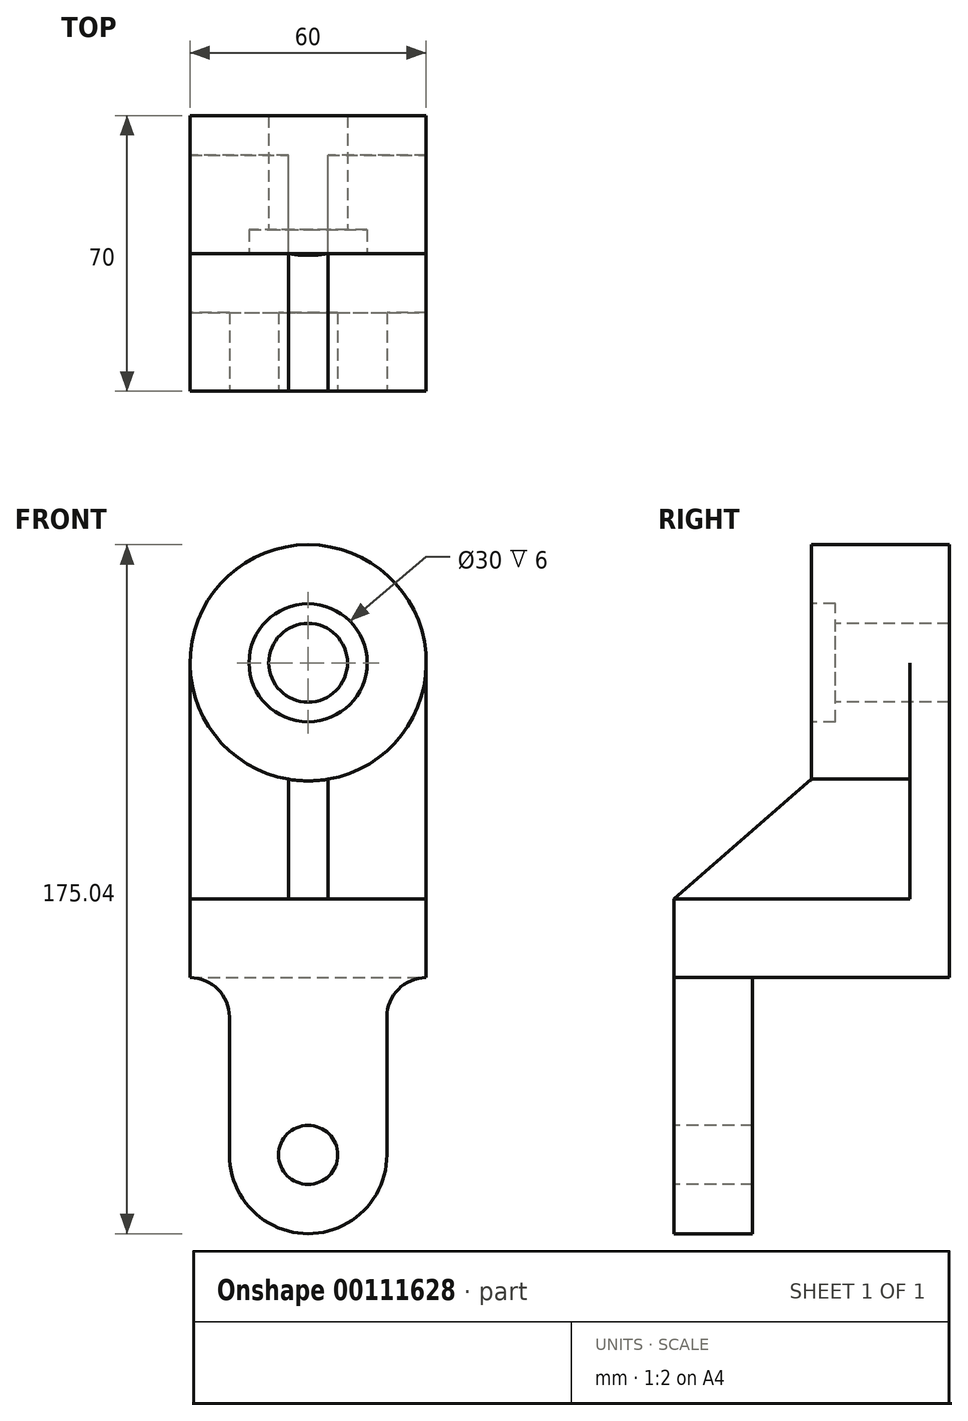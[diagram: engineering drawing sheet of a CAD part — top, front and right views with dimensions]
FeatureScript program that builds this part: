
annotation { "Feature Type Name" : "Feature", "Feature Type Description" : "" }
export const myFeature = defineFeature(function(context is Context, id is Id, definition is map)
    precondition{}
    {
        {
            var Q0;
            Q0=qCreatedBy(makeId("Top.planeOp"),FACE);
            var sketch = newSketch(context, id + "F0", { "sketchPlane" : qUnion([Q0])});
            skLineSegment(sketch, "E0.bottom", {"start": v(-34.23, 8.14) * mm, "end": v(25.77, 8.14) * mm});
            skLineSegment(sketch, "E0.top", {"start": v(-34.23, -61.86) * mm, "end": v(25.77, -61.86) * mm});
            skLineSegment(sketch, "E0.left", {"start": v(-34.23, 8.14) * mm, "end": v(-34.23, -61.86) * mm});
            skLineSegment(sketch, "E0.right", {"start": v(25.77, 8.14) * mm, "end": v(25.77, -61.86) * mm});
            skPoint(sketch, "E1", {"position": v(-4.23, 8.14) * mm});
            skSolve(sketch);
        }
        {
            var Q0;
            Q0 = qSketchRegion(id + "F0", true);
            extrude(context, id + "F1", {"entities" : qUnion([Q0]), "depth" : 20 * mm});
        }
        {
            var Q0;
            Q0=makeQuery(id+"F1.opExtrude","SWEPT_FACE",FACE,{"disambiguationData":[OSD([sQuery(id+"F0.wireOp",EDGE,"E0.bottom")])]});
            var sketch = newSketch(context, id + "F2", { "sketchPlane" : qUnion([Q0])});
            skPoint(sketch, "E2", {"position": v(4.23, 0) * mm});
            skLineSegment(sketch, "E3", {"start": v(-25.77, 20) * mm, "end": v(-25.77, 80) * mm});
            skLineSegment(sketch, "E4", {"start": v(34.23, 20) * mm, "end": v(34.23, 80) * mm});
            skLineSegment(sketch, "E5", {"start": v(-25.77, 20) * mm, "end": v(34.23, 20) * mm});
            skArc(sketch, "E6", {"start": v(34.23, 80) * mm, "mid": v(4.23, 110) * mm, "end": v(-25.77, 80) * mm});
            skSolve(sketch);
        }
        {
            var Q0;
            Q0 = qSketchRegion(id + "F2", true);
            extrude(context, id + "F3", {"entities" : qUnion([Q0]), "operationType" : NewBodyOperationType.ADD, "oppositeDirection" : true, "depth" : 10 * mm});
        }
        {
            var Q0;
            Q0=makeQuery(id+"F3.opExtrude","CAP_FACE",FACE,{"disambiguationData":[OSD([sQuery(id+"F2.wireOp",EDGE,"E3"),sQuery(id+"F2.wireOp",EDGE,"E4"),sQuery(id+"F2.wireOp",EDGE,"E5"),sQuery(id+"F2.wireOp",EDGE,"E6")])],"isStart":false});
            var sketch = newSketch(context, id + "F4", { "sketchPlane" : qUnion([Q0])});
            skPoint(sketch, "E7", {"position": v(-4.23, 80) * mm});
            skCircle(sketch, "E8", {"center": v(-4.23, 80) * mm, "radius": 30 * mm});
            skSolve(sketch);
        }
        {
            var Q0;
            Q0 = qSketchRegion(id + "F4", true);
            extrude(context, id + "F5", {"entities" : qUnion([Q0]), "operationType" : NewBodyOperationType.ADD, "depth" : 25 * mm});
        }
        {
            var Q0;
            Q0=makeQuery(id+"F5.opExtrude","CAP_FACE",FACE,{"disambiguationData":[OSD([sQuery(id+"F4.wireOp",EDGE,"E8")])],"isStart":false});
            var sketch = newSketch(context, id + "F6", { "sketchPlane" : qUnion([Q0])});
            skPoint(sketch, "E9", {"position": v(-4.23, 80) * mm});
            skSolve(sketch);
        }
        {
            var Q0;
            Q0=sQuery(id+"F6.wireOp",VERTEX,"E9");
            var Q1;
            Q1=makeQuery(id+"F1.opExtrude","SWEPT_BODY",BODY,{"disambiguationData":[OSD([sQuery(id+"F0.wireOp",EDGE,"E0.bottom"),sQuery(id+"F0.wireOp",EDGE,"E0.top"),sQuery(id+"F0.wireOp",EDGE,"E0.left"),sQuery(id+"F0.wireOp",EDGE,"E0.right")])]});
            hole(context, id + "F7", {"style" : HoleStyle.C_BORE, "endStyle" : HoleEndStyle.BLIND, "holeDiameter" : 20 * mm, "cBoreDiameter" : 30 * mm, "cBoreDepth" : 6 * mm, "holeDepth" : 50 * mm, "startFromSketch" : true, "locations" : qUnion([Q0]), "scope" : qUnion([Q1])});
        }
        {
            var Q0;
            Q0=makeQuery(id+"F1.opExtrude","CAP_FACE",FACE,{"disambiguationData":[OSD([sQuery(id+"F0.wireOp",EDGE,"E0.bottom"),sQuery(id+"F0.wireOp",EDGE,"E0.top"),sQuery(id+"F0.wireOp",EDGE,"E0.left"),sQuery(id+"F0.wireOp",EDGE,"E0.right")])],"isStart":false});
            var sketch = newSketch(context, id + "F8", { "sketchPlane" : qUnion([Q0])});
            skPoint(sketch, "E10.endSnap0", {"position": v(-4.23, -61.86) * mm});
            skLineSegment(sketch, "E11.bottom", {"start": v(0.77, -61.86) * mm, "end": v(-9.23, -61.86) * mm});
            skLineSegment(sketch, "E11.top", {"start": v(0.77, -1.86) * mm, "end": v(-9.23, -1.86) * mm});
            skLineSegment(sketch, "E11.left", {"start": v(0.77, -61.86) * mm, "end": v(0.77, -1.86) * mm});
            skLineSegment(sketch, "E11.right", {"start": v(-9.23, -61.86) * mm, "end": v(-9.23, -1.86) * mm});
            skSolve(sketch);
        }
        {
            var Q0;
            Q0 = qSketchRegion(id + "F8", true);
            var Q1;
            Q1=makeQuery(id+"F5.boolean.opBoolean","MERGE",FACE,{"derivedFrom":[makeQuery(id+"F3.opExtrude","SWEPT_FACE",FACE,{"disambiguationData":[OSD([sQuery(id+"F2.wireOp",EDGE,"E6")])]}),makeQuery(id+"F5.opExtrude","SWEPT_FACE",FACE,{"disambiguationData":[OSD([sQuery(id+"F4.wireOp",EDGE,"E8")])]})]});
            extrude(context, id + "F9", {"entities" : qUnion([Q0]), "operationType" : NewBodyOperationType.ADD, "endBound" : BoundingType.UP_TO_SURFACE, "endBoundEntityFace" : qUnion([Q1]), "depth" : 30 * mm});
        }
        {
            var Q0;
            Q0=makeQuery(id+"F9.opExtrude","SWEPT_FACE",FACE,{"disambiguationData":[OSD([sQuery(id+"F8.wireOp",EDGE,"E11.left")])]});
            var sketch = newSketch(context, id + "F10", { "sketchPlane" : qUnion([Q0])});
            skLineSegment(sketch, "E12", {"start": v(-61.86, 20) * mm, "end": v(-61.86, 50.42) * mm});
            skLineSegment(sketch, "E13", {"start": v(-61.86, 50.42) * mm, "end": v(-26.86, 50.42) * mm});
            skLineSegment(sketch, "E14", {"start": v(-26.86, 50.42) * mm, "end": v(-61.86, 20) * mm});
            skSolve(sketch);
        }
        {
            var Q0;
            Q0=makeQuery(id+"F0.imprint","IMPRINT",FACE,{"disambiguationData":[TD([[makeQuery(id+"F0.imprint","IMPRINT",EDGE,{"derivedFrom":sQuery(id+"F0.wireOp",EDGE,"E0.bottom")}),-1.0]])]});
            var sketch = newSketch(context, id + "F11", { "sketchPlane" : qUnion([Q0])});
            skLineSegment(sketch, "E15.bottom", {"start": v(-34.23, -61.86) * mm, "end": v(25.77, -61.86) * mm});
            skLineSegment(sketch, "E15.top", {"start": v(-34.23, -41.86) * mm, "end": v(25.77, -41.86) * mm});
            skLineSegment(sketch, "E15.left", {"start": v(-34.23, -61.86) * mm, "end": v(-34.23, -41.86) * mm});
            skLineSegment(sketch, "E15.right", {"start": v(25.77, -61.86) * mm, "end": v(25.77, -41.86) * mm});
            skLineSegment(sketch, "E16.bottom", {"start": v(24.1, -41.86) * mm, "end": v(22.4, -41.86) * mm});
            skLineSegment(sketch, "E16.top", {"start": v(24.1, -41.86) * mm, "end": v(22.4, -41.86) * mm});
            skLineSegment(sketch, "E16.left", {"start": v(24.1, -41.86) * mm, "end": v(24.1, -41.86) * mm});
            skSolve(sketch);
        }
        {
            var Q0;
            Q0 = qSketchRegion(id + "F11", true);
            extrude(context, id + "F12", {"entities" : qUnion([Q0]), "operationType" : NewBodyOperationType.ADD, "oppositeDirection" : true, "depth" : 45 * mm});
        }
        {
            var Q0;
            Q0=makeQuery(id+"F12.boolean.opBoolean","MERGE",FACE,{"derivedFrom":[makeQuery(id+"F1.opExtrude","SWEPT_FACE",FACE,{"disambiguationData":[OSD([sQuery(id+"F0.wireOp",EDGE,"E0.top")])]}),makeQuery(id+"F12.opExtrude","SWEPT_FACE",FACE,{"disambiguationData":[OSD([sQuery(id+"F11.wireOp",EDGE,"E15.bottom")])]})]});
            var sketch = newSketch(context, id + "F13", { "sketchPlane" : qUnion([Q0])});
            skSolve(sketch);
        }
        {
            var Q0;
            {var subQ0=sQuery(id+"F0.wireOp",EDGE,"E0.top");Q0=makeQuery(id+"F13.imprint","IMPRINT",FACE,{"disambiguationData":[TD([[makeQuery(id+"F13.imprint","IMPRINT",EDGE,{"derivedFrom":makeQuery(id+"F1.opExtrude","CAP_EDGE",EDGE,{"disambiguationData":[OSD([subQ0])],"isStart":false})}),-1.0]])]});}
            var sketch = newSketch(context, id + "F14", { "sketchPlane" : qUnion([Q0])});
            skLineSegment(sketch, "E17", {"start": v(-34.23, 0) * mm, "end": v(-24.23, 0) * mm});
            skLineSegment(sketch, "E18", {"start": v(-24.23, 0) * mm, "end": v(-24.23, -45) * mm});
            skLineSegment(sketch, "E19", {"start": v(-24.23, -45) * mm, "end": v(15.77, -45) * mm});
            skLineSegment(sketch, "E20", {"start": v(15.77, -45) * mm, "end": v(15.77, 0) * mm});
            skLineSegment(sketch, "E21", {"start": v(15.77, 0) * mm, "end": v(25.77, 0) * mm});
            skLineSegment(sketch, "E22", {"start": v(-34.23, 0) * mm, "end": v(-34.23, -45) * mm});
            skLineSegment(sketch, "E23", {"start": v(-34.23, -45) * mm, "end": v(-24.23, -45) * mm});
            skLineSegment(sketch, "E24", {"start": v(25.77, 0) * mm, "end": v(25.77, -45) * mm});
            skLineSegment(sketch, "E25", {"start": v(25.77, -45) * mm, "end": v(15.77, -45) * mm});
            skSolve(sketch);
        }
        {
            var Q0;
            Q0 = qSketchRegion(id + "F14", true);
            extrude(context, id + "F15", {"entities" : qUnion([Q0]), "operationType" : NewBodyOperationType.REMOVE, "oppositeDirection" : true, "depth" : 20 * mm});
        }
        {
            var Q0;
            {var subQ0=sQuery(id+"F0.wireOp",EDGE,"E0.top");Q0=makeQuery(id+"F13.imprint","IMPRINT",FACE,{"disambiguationData":[TD([[makeQuery(id+"F13.imprint","IMPRINT",EDGE,{"derivedFrom":makeQuery(id+"F1.opExtrude","CAP_EDGE",EDGE,{"disambiguationData":[OSD([subQ0])],"isStart":false})}),-1.0]])]});}
            var sketch = newSketch(context, id + "F16", { "sketchPlane" : qUnion([Q0])});
            skArc(sketch, "E26", {"start": v(-24.23, -45) * mm, "mid": v(-4.23, -65.04) * mm, "end": v(15.77, -45) * mm});
            skLineSegment(sketch, "E27", {"start": v(-24.23, -45) * mm, "end": v(15.77, -45) * mm});
            skSolve(sketch);
        }
        {
            var Q0;
            Q0 = qSketchRegion(id + "F16", true);
            extrude(context, id + "F17", {"entities" : qUnion([Q0]), "operationType" : NewBodyOperationType.ADD, "oppositeDirection" : true, "depth" : 20 * mm});
        }
        {
            var Q0;
            Q0=makeQuery(id+"F17.boolean.opBoolean","MERGE",FACE,{"derivedFrom":[makeQuery(id+"F12.boolean.opBoolean","MERGE",FACE,{"derivedFrom":[makeQuery(id+"F1.opExtrude","SWEPT_FACE",FACE,{"disambiguationData":[OSD([sQuery(id+"F0.wireOp",EDGE,"E0.top")])]}),makeQuery(id+"F12.opExtrude","SWEPT_FACE",FACE,{"disambiguationData":[OSD([sQuery(id+"F11.wireOp",EDGE,"E15.bottom")])]})]}),makeQuery(id+"F17.opExtrude","CAP_FACE",FACE,{"disambiguationData":[OSD([sQuery(id+"F16.wireOp",EDGE,"E26"),sQuery(id+"F16.wireOp",EDGE,"E27")])],"isStart":true})]});
            var sketch = newSketch(context, id + "F18", { "sketchPlane" : qUnion([Q0])});
            skPoint(sketch, "E28", {"position": v(-4.23, -45.04) * mm});
            skSolve(sketch);
        }
        {
            var Q0;
            Q0=sQuery(id+"F18.wireOp",VERTEX,"E28");
            var Q1;
            Q1=makeQuery(id+"F1.opExtrude","SWEPT_BODY",BODY,{"disambiguationData":[OSD([sQuery(id+"F0.wireOp",EDGE,"E0.bottom"),sQuery(id+"F0.wireOp",EDGE,"E0.top"),sQuery(id+"F0.wireOp",EDGE,"E0.left"),sQuery(id+"F0.wireOp",EDGE,"E0.right")])]});
            hole(context, id + "F19", {"style" : HoleStyle.SIMPLE, "endStyle" : HoleEndStyle.BLIND, "holeDiameter" : 15 * mm, "holeDepth" : 50 * mm, "startFromSketch" : true, "locations" : qUnion([Q0]), "scope" : qUnion([Q1])});
        }
        {
            var Q0;
            Q0=makeQuery(id+"F15.boolean.opBoolean","COPY",EDGE,{"derivedFrom":makeQuery(id+"F15.opExtrude","SWEPT_EDGE",EDGE,{"disambiguationData":[OSD([sQuery(id+"F14.wireOp",EDGE,"E20"),sQuery(id+"F14.wireOp",EDGE,"E21")])]})});
            var Q1;
            Q1=makeQuery(id+"F15.boolean.opBoolean","COPY",EDGE,{"derivedFrom":makeQuery(id+"F15.opExtrude","SWEPT_EDGE",EDGE,{"disambiguationData":[OSD([sQuery(id+"F14.wireOp",EDGE,"E17"),sQuery(id+"F14.wireOp",EDGE,"E18")])]})});
            fillet(context, id + "F20", {"entities" : qUnion([Q0, Q1]), "radius" : 10 * mm, "tangentPropagation" : true, "allowEdgeOverflow" : false});
        }
        {
            var Q0;
            Q0 = qSketchRegion(id + "F10", true);
            extrude(context, id + "F21", {"entities" : qUnion([Q0]), "operationType" : NewBodyOperationType.REMOVE, "oppositeDirection" : true, "depth" : 25 * mm});
        }
    });
